# Revit family: Reece_Tap_Roca_T 1000_Shower Mixer_Thermostatic with Diverter
name_source: partatom
category: Plumbing Fixtures
revit_build: Autodesk Revit 2018 (Build: 20190510_1515(x64)
units: mm (PartAtom-declared; Revit-internal decimal feet)

## family parameters
Cut with Voids When Loaded = No
Host = Face
Part Type = Normal
Room Calculation Point = Yes
Round Connector Dimension = Use Diameter
Shared = Yes

## types (1)
- Chrome
    CWFU = 0
    Default Elevation = 1000 mm  [stored 3.28084 ft]
    Description = Roca T-1000 Concealed Thermostatic Shower Mixer Tap with Diverter Chrome
    Disclaimer = THIS FILE IS THE PROPERTY OF THE REECE GROUP. IT MAY NOT BE REPRODUCED, REVERSE-ENGINEERED OR MODIFIED. ANY REPUBLICATION, TRANSMISSION OR DISTRIBUTION FOR THE PURPOSE OF COMMERCIALLY EXPLOITING THE FILES IS PROHIBITED.
    HWFU = 0
    Keynote = Product #9508626, Reece_Tap_Roca_T 1000_Shower Mixer_Thermostatic with Diverter - Chrome
    Manufacturer = Roca
    Model = T-1000
    Reece_Detail_Additional = Thermostatic/Diverter Shower Mixer
    Reece_Detail_Disclaimer = THIS FILE IS THE PROPERTY OF THE REECE GROUP. IT MAY NOT BE REPRODUCED, REVERSE-ENGINEERED OR MODIFIED. ANY REPUBLICATION, TRANSMISSION OR DISTRIBUTION FOR THE PURPOSE OF COMMERCIALLY EXPLOITING THE FILES IS PROHIBITED.
    Reece_Material-Main = Reece_Brass_Chrome
    Reece_Material_Tap_Cold = Reece_Metal_Hard Graphite
    Reece_Material_Tap_Hot = Render_Hot_Water_Cap
    Reece_Mixer_Inlet = 19 mm  [stored 0.062336 ft]
    Reece_Overall_Length = 160 mm  [stored 0.524934 ft]
    Reece_Overall_Projection = 78 mm  [stored 0.255906 ft]
    Reece_Overall_Width = 160 mm  [stored 0.524934 ft]
    Reece_Product_Brand = Roca
    Reece_Product_Description = Roca T-1000 Concealed Thermostatic Shower Mixer Tap with Diverter Chrome
    Reece_Product_Mount = Wall Mounted
    Reece_Product_Number = 9508626
    Reece_Product_Sub Brand = T-1000
    Reece_Product_Type = Tap
    Reece_Product_Web Page = https://www.reece.com.au
    Type Comments = Tap
    URL = https://www.reece.com.au
    WFU = 0

note: [stored X ft] marks values corroborated as IEEE doubles in the binary element streams (Revit-internal decimal feet)

## geometry (parser evidence)
native form markers: Sweep x1
no freeform markers — native parametric forms only
